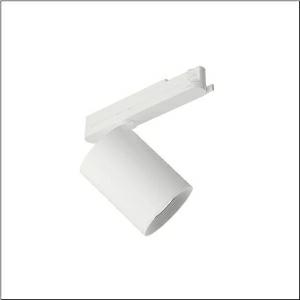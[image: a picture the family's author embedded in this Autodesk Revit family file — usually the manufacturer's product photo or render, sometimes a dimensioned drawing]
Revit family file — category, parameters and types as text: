
# Revit family: spot_11_51sd14ebb5a
name_source: partatom
category: Lighting Fixtures
units: mm (PartAtom-declared; Revit-internal decimal feet)

## family parameters
Cut with Voids When Loaded = No
Host = Face
Light Source = No
Part Type = Normal
Room Calculation Point = No
Round Connector Dimension = Use Diameter
Shared = No

## types (1)
- --- (1 x LED, 7340 lm, 51 W, 3000K)
    Apparent Load = 51 VA
    CIE Flux Codes = 95 98 100 100 100
    Color Rendering = 90
    Color Temperature = 3000K
    Default Elevation = 1800 mm
    Description = Spot 11, directional spotlight, light control with lens, of PMMA, LED rated luminous flux: 5.630lm, light colour: 930, control gear: ECG Multilumen, with 3-phase adapter, mains connection: 220..240V, AC, 50/60Hz, of aluminium, traffic white (RAL 9016), length: 253mm, diameter: 105mm, protection rating (complete): IP20, insulation class (complete): insulation class I (protective earthing), certification: CE, impact resistance: IK02, permissible ambient temperature for indoor applications: -20..+40°C, packaging unit: 1 piece
    Height = 175 mm
    Lamp = 1 x LED
    Lamp Light Flux = 7340 lm
    Lamp Power = 51 W
    Lamp count = 1
    Length = 105 mm
    Luminous efficacy = 144 lm/W
    Manufacturer = Siteco
    ModVariant = No
    Model = 51SD14EBB5A
    Mounting Place = Ceiling
    Mounting Type = Pendant
    Number of Poles = 1
    OnlyDefault = Yes
    Power Factor = 1
    Product Name = Spot 11
    Product group = directional spotlight
    ProductGroupID = 905
    Protection Class = Protection class I
    Protection Degree = IP 20
    RLX_Detail_Level = 1
    RLX_Emergency_Light_Flux = 0 lm
    RLX_Emergency_Type = 0
    RLX_Emergency_Type_DB = No
    RlxData = <blob elided: 17685 chars, md5=f4b68a2c>
    Socket = socket
    Standby Power = 0 W
    System Light Flux = 7340 lm
    System Power = 51 W
    Type Comments = factory setting: luminous flux: 100 % | (ON | ON | ON | ON) | 1050 mA
    Type Image = l_1006697.jpg
    URL = http://relux.com
    VarID = @adj_146905
    Voltage = 0 V
    Weight = 0.00 kg
    Width = 0 mm  [stored 0 ft]

note: [stored X ft] marks values corroborated as IEEE doubles in the binary element streams (Revit-internal decimal feet)

## geometry (parser evidence)
native form markers: Blend x4, Sweep x10
no freeform markers — native parametric forms only
